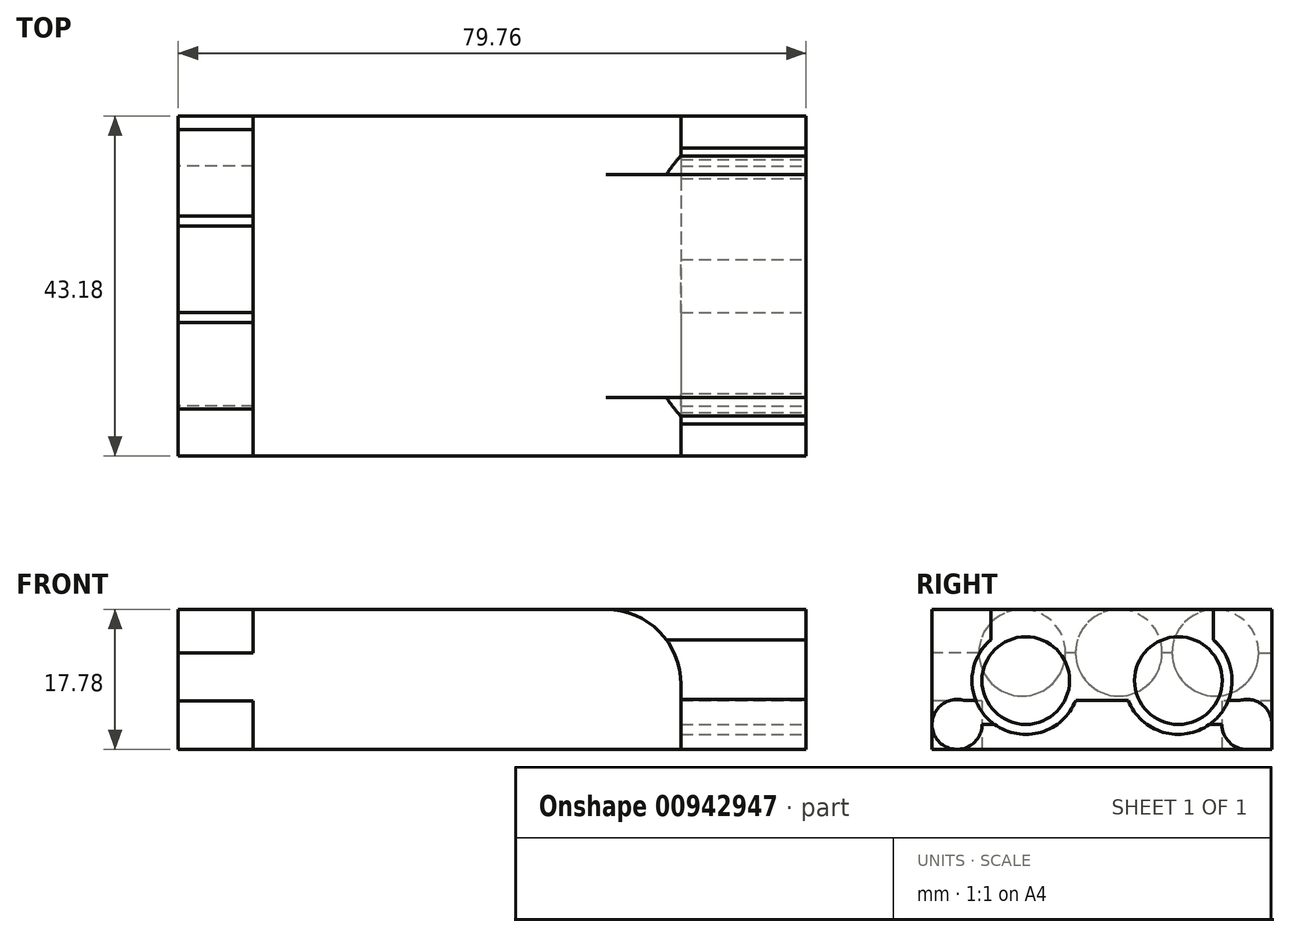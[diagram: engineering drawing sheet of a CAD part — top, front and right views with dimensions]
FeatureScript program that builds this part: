
annotation { "Feature Type Name" : "Feature", "Feature Type Description" : "" }
export const myFeature = defineFeature(function(context is Context, id is Id, definition is map)
    precondition{}
    {
        {
            var Q0;
            Q0=qCreatedBy(makeId("Top.planeOp"),FACE);
            var sketch = newSketch(context, id + "F0", { "sketchPlane" : qUnion([Q0])});
            skLineSegment(sketch, "E0", {"start": v(-39.88, 0) * mm, "end": v(-39.88, 21.59) * mm});
            skLineSegment(sketch, "E1.MirrorCS", {"start": v(39.88, 0) * mm, "end": v(39.88, 21.59) * mm});
            skLineSegment(sketch, "E2.MirrorCS", {"start": v(-39.88, 0) * mm, "end": v(-39.88, -21.59) * mm});
            skLineSegment(sketch, "E3.MirrorCS", {"start": v(39.88, 0) * mm, "end": v(39.88, -21.59) * mm});
            skLineSegment(sketch, "E4", {"start": v(-39.88, 21.59) * mm, "end": v(39.88, 21.59) * mm});
            skLineSegment(sketch, "E5", {"start": v(39.88, -21.59) * mm, "end": v(-39.88, -21.59) * mm});
            skSolve(sketch);
        }
        {
            var Q0;
            Q0=makeQuery(id+"F0.imprint","IMPRINT",FACE,{"disambiguationData":[TD([[makeQuery(id+"F0.imprint","IMPRINT",EDGE,{"derivedFrom":sQuery(id+"F0.wireOp",EDGE,"E0")}),-1.0]])]});
            extrude(context, id + "F1", {"entities" : qUnion([Q0]), "depth" : 17.78 * mm, "offsetDistance" : 25.4 * mm});
        }
        {
            var Q0;
            Q0=makeQuery(id+"F1.opExtrude","SWEPT_FACE",FACE,{"disambiguationData":[OSD([sQuery(id+"F0.wireOp",EDGE,"E0"),sQuery(id+"F0.wireOp",EDGE,"E2.MirrorCS")])]});
            var sketch = newSketch(context, id + "F2", { "sketchPlane" : qUnion([Q0])});
            skLineSegment(sketch, "E6", {"start": v(-21.59, 0) * mm, "end": v(21.59, 0) * mm});
            skLineSegment(sketch, "E7", {"start": v(-21.59, 17.78) * mm, "end": v(-21.59, 12.28) * mm});
            skCircle(sketch, "E8", {"center": v(-14.4, 12.28) * mm, "radius": 5.5 * mm});
            skLineSegment(sketch, "E9", {"start": v(-19.9, 12.28) * mm, "end": v(-21.59, 12.28) * mm});
            skLineSegment(sketch, "E10", {"start": v(13.1, 12.28) * mm, "end": v(21.59, 12.28) * mm});
            skLineSegment(sketch, "E11", {"start": v(-21.59, 0) * mm, "end": v(-21.59, 6.14) * mm});
            skLineSegment(sketch, "E12", {"start": v(-21.59, 6.14) * mm, "end": v(21.59, 6.14) * mm});
            skLineSegment(sketch, "E13", {"start": v(-21.59, 6.14) * mm, "end": v(-15.24, 6.14) * mm});
            skLineSegment(sketch, "E14.MirrorCS", {"start": v(21.59, 0) * mm, "end": v(21.59, 6.14) * mm});
            skLineSegment(sketch, "E15.MirrorCS", {"start": v(21.59, 6.14) * mm, "end": v(-21.59, 6.14) * mm});
            skLineSegment(sketch, "E16", {"start": v(21.59, 6.14) * mm, "end": v(15.24, 6.14) * mm});
            skLineSegment(sketch, "E17", {"start": v(-15.24, 6.14) * mm, "end": v(-15.24, 0) * mm});
            skLineSegment(sketch, "E18.MirrorCS", {"start": v(15.24, 6.14) * mm, "end": v(15.24, 0) * mm});
            skLineSegment(sketch, "E19", {"start": v(-8.9, 12.28) * mm, "end": v(-7.63, 12.28) * mm});
            skCircle(sketch, "E20.MirrorC", {"center": v(-2.13, 12.28) * mm, "radius": 5.5 * mm});
            skCircle(sketch, "E21.MirrorC", {"center": v(10.14, 12.28) * mm, "radius": 5.5 * mm});
            skLineSegment(sketch, "E22", {"start": v(3.37, 12.28) * mm, "end": v(4.64, 12.28) * mm});
            skSolve(sketch);
        }
        {
            var Q0;
            {var subQ0=sQuery(id+"F2.wireOp",EDGE,"E7");Q0=makeQuery(id+"F2.imprint","IMPRINT",FACE,{"disambiguationData":[TD([[makeQuery(id+"F2.imprint","IMPRINT",EDGE,{"derivedFrom":subQ0}),1.0]])]});}
            var Q1;
            {var subQ0=sQuery(id+"F2.wireOp",EDGE,"11ba6505-8bd9-4545-8600-2fb35892f41e0.MirrorC");var subQ1=sQuery(id+"F2.wireOp",EDGE,"E8");var subQ2=makeQuery(id+"F2.imprint","INTERSECT",VERTEX,{"derivedFrom":[subQ1,subQ0]});Q1=makeQuery(id+"F2.imprint","IMPRINT",FACE,{"disambiguationData":[TD([[makeQuery(id+"F2.imprint","IMPRINT",EDGE,{"disambiguationData":[TD([[subQ2,-1.0]])],"derivedFrom":subQ1}),-1.0]])]});}
            var Q2;
            {var subQ0=sQuery(id+"F2.wireOp",EDGE,"8c5e6d80-e282-41b0-858f-738f4d739d140.MirrorC");var subQ1=sQuery(id+"F2.wireOp",EDGE,"11ba6505-8bd9-4545-8600-2fb35892f41e0.MirrorC");var subQ2=makeQuery(id+"F2.imprint","INTERSECT",VERTEX,{"derivedFrom":[subQ1,subQ0]});Q2=makeQuery(id+"F2.imprint","IMPRINT",FACE,{"disambiguationData":[TD([[makeQuery(id+"F2.imprint","IMPRINT",EDGE,{"disambiguationData":[TD([[subQ2,1.0]])],"derivedFrom":subQ1}),1.0]])]});}
            var Q3;
            {var subQ0=sQuery(id+"F2.wireOp",EDGE,"E10");Q3=makeQuery(id+"F2.imprint","IMPRINT",FACE,{"disambiguationData":[TD([[makeQuery(id+"F2.imprint","IMPRINT",EDGE,{"derivedFrom":subQ0}),1.0]])]});}
            var Q4;
            {var subQ0=sQuery(id+"F2.wireOp",EDGE,"E11");Q4=makeQuery(id+"F2.imprint","IMPRINT",FACE,{"disambiguationData":[TD([[makeQuery(id+"F2.imprint","IMPRINT",EDGE,{"derivedFrom":subQ0}),1.0]])]});}
            var Q5;
            {var subQ0=sQuery(id+"F2.wireOp",EDGE,"E14.MirrorCS");Q5=makeQuery(id+"F2.imprint","IMPRINT",FACE,{"disambiguationData":[TD([[makeQuery(id+"F2.imprint","IMPRINT",EDGE,{"derivedFrom":subQ0}),-1.0]])]});}
            var Q6;
            {var subQ0=sQuery(id+"F2.wireOp",EDGE,"E22");Q6=makeQuery(id+"F2.imprint","IMPRINT",FACE,{"disambiguationData":[TD([[makeQuery(id+"F2.imprint","IMPRINT",EDGE,{"derivedFrom":subQ0}),1.0]])]});}
            extrude(context, id + "F3", {"entities" : qUnion([Q0, Q1, Q2, Q3, Q4, Q5, Q6]), "operationType" : NewBodyOperationType.REMOVE, "oppositeDirection" : true, "depth" : 9.52 * mm, "offsetDistance" : 25.4 * mm});
        }
        {
            var Q0;
            {var subQ0=sQuery(id+"F2.wireOp",EDGE,"E17");Q0=makeQuery(id+"F2.imprint","IMPRINT",FACE,{"disambiguationData":[TD([[makeQuery(id+"F2.imprint","IMPRINT",EDGE,{"derivedFrom":subQ0}),1.0]])]});}
            var Q1;
            {var subQ0=sQuery(id+"F2.wireOp",EDGE,"E9");Q1=makeQuery(id+"F2.imprint","IMPRINT",FACE,{"disambiguationData":[TD([[makeQuery(id+"F2.imprint","IMPRINT",EDGE,{"derivedFrom":subQ0}),1.0]])]});}
            extrude(context, id + "F4", {"entities" : qUnion([Q0, Q1]), "operationType" : NewBodyOperationType.REMOVE, "oppositeDirection" : true, "depth" : 3 / 406.4 * mm, "offsetDistance" : 25.4 * mm});
        }
        {
            var Q0;
            Q0=makeQuery(id+"F1.opExtrude","SWEPT_FACE",FACE,{"disambiguationData":[OSD([sQuery(id+"F0.wireOp",EDGE,"E1.MirrorCS"),sQuery(id+"F0.wireOp",EDGE,"E3.MirrorCS")])]});
            var sketch = newSketch(context, id + "F5", { "sketchPlane" : qUnion([Q0])});
            skLineSegment(sketch, "E23", {"start": v(-21.59, 0) * mm, "end": v(-21.59, 3.18) * mm});
            skLineSegment(sketch, "E24", {"start": v(-21.59, 0) * mm, "end": v(-12.04, 0) * mm});
            skLineSegment(sketch, "E25", {"start": v(-21.59, 0) * mm, "end": v(21.59, 0) * mm});
            skLineSegment(sketch, "E26", {"start": v(21.59, 0) * mm, "end": v(-21.59, 0) * mm});
            skLineSegment(sketch, "E27", {"start": v(-21.59, 3.18) * mm, "end": v(-18.41, 3.18) * mm});
            skCircle(sketch, "E28", {"center": v(-18.41, 3.18) * mm, "radius": 3.18 * mm});
            skLineSegment(sketch, "E29", {"start": v(-15.24, 3.18) * mm, "end": v(-13.65, 3.18) * mm});
            skCircle(sketch, "E30", {"center": v(-9.69, 8.74) * mm, "radius": 5.57 * mm});
            skCircle(sketch, "E31.MirrorC", {"center": v(9.69, 8.74) * mm, "radius": 5.57 * mm});
            skArc(sketch, "E32", {"start": v(-3.34, 11.27) * mm, "mid": v(-16.52, 8.74) * mm, "end": v(-3.34, 6.21) * mm});
            skArc(sketch, "E33.MirrorC", {"start": v(3.34, 11.27) * mm, "mid": v(16.52, 8.74) * mm, "end": v(3.34, 6.21) * mm});
            skCircle(sketch, "E34.MirrorC", {"center": v(18.41, 3.18) * mm, "radius": 3.18 * mm});
            skLineSegment(sketch, "E35", {"start": v(-3.34, 6.21) * mm, "end": v(3.34, 6.21) * mm});
            skLineSegment(sketch, "E36", {"start": v(-9.69, 8.74) * mm, "end": v(-6.73, 8.74) * mm});
            skLineSegment(sketch, "E37.MirrorCS", {"start": v(-3.34, 11.27) * mm, "end": v(3.34, 11.27) * mm});
            skLineSegment(sketch, "E38", {"start": v(-14.14, 13.93) * mm, "end": v(-14.14, 17.78) * mm});
            skLineSegment(sketch, "E39.MirrorCS", {"start": v(14.14, 13.93) * mm, "end": v(14.14, 17.78) * mm});
            skPoint(sketch, "E40.trimOffspring.end.orphan", {"position": v(-9.68, 3.19) * mm});
            skLineSegment(sketch, "E41.MirrorCS", {"start": v(15.24, 3.18) * mm, "end": v(13.65, 3.18) * mm});
            skLineSegment(sketch, "E42", {"start": v(-17.52, 6.22) * mm, "end": v(-16.04, 6.22) * mm});
            skLineSegment(sketch, "E43.MirrorCS", {"start": v(17.52, 6.22) * mm, "end": v(16.04, 6.22) * mm});
            skSolve(sketch);
        }
        {
            var Q0;
            {var subQ1=sQuery(id+"F5.wireOp",EDGE,"E37.MirrorCS");Q0=makeQuery(id+"F5.imprint","IMPRINT",FACE,{"disambiguationData":[TD([[makeQuery(id+"F5.imprint","IMPRINT",EDGE,{"derivedFrom":subQ1}),1.0]])]});}
            var Q1;
            Q1=makeQuery(id+"F5.imprint","IMPRINT",FACE,{"disambiguationData":[TD([[makeQuery(id+"F5.imprint","IMPRINT",EDGE,{"derivedFrom":sQuery(id+"F5.wireOp",EDGE,"E30")}),-1.0]])]});
            extrude(context, id + "F6", {"entities" : qUnion([Q0, Q1]), "operationType" : NewBodyOperationType.REMOVE, "oppositeDirection" : true, "depth" : 3 / 406.4 * mm, "offsetDistance" : 25.4 * mm});
        }
        {
            var Q0;
            {var subQ0=sQuery(id+"F5.wireOp",EDGE,"E29");Q0=makeQuery(id+"F5.imprint","IMPRINT",FACE,{"disambiguationData":[TD([[makeQuery(id+"F5.imprint","IMPRINT",EDGE,{"derivedFrom":subQ0}),-1.0]])]});}
            extrude(context, id + "F7", {"entities" : qUnion([Q0]), "operationType" : NewBodyOperationType.REMOVE, "oppositeDirection" : true, "depth" : 17.46 * mm, "offsetDistance" : 25.4 * mm});
        }
        {
            var Q0;
            {var subQ1=sQuery(id+"F5.wireOp",EDGE,"E38");Q0=makeQuery(id+"F5.imprint","IMPRINT",FACE,{"disambiguationData":[TD([[makeQuery(id+"F5.imprint","IMPRINT",EDGE,{"derivedFrom":subQ1}),1.0]])]});}
            var Q1;
            {var subQ5=sQuery(id+"F5.wireOp",EDGE,"E39.MirrorCS");Q1=makeQuery(id+"F5.imprint","IMPRINT",FACE,{"disambiguationData":[TD([[makeQuery(id+"F5.imprint","IMPRINT",EDGE,{"derivedFrom":subQ5}),-1.0]])]});}
            extrude(context, id + "F8", {"entities" : qUnion([Q0, Q1]), "operationType" : NewBodyOperationType.REMOVE, "oppositeDirection" : true, "depth" : 25.4 * mm, "offsetDistance" : 25.4 * mm});
        }
        {
            var Q0;
            {var subQ0=sQuery(id+"F5.wireOp",EDGE,"E23");Q0=makeQuery(id+"F5.imprint","IMPRINT",FACE,{"disambiguationData":[TD([[makeQuery(id+"F5.imprint","IMPRINT",EDGE,{"derivedFrom":subQ0}),1.0]])]});}
            var Q1;
            {var subQ0=sQuery(id+"F5.wireOp",EDGE,"E26");var subQ3=sQuery(id+"F5.wireOp",EDGE,"E34.MirrorC");var subQ4=makeQuery(id+"F5.imprint","INTERSECT",VERTEX,{"derivedFrom":[subQ0,subQ3]});Q1=makeQuery(id+"F5.imprint","IMPRINT",FACE,{"disambiguationData":[TD([[makeQuery(id+"F5.imprint","IMPRINT",EDGE,{"disambiguationData":[TD([[subQ4,1.0]])],"derivedFrom":subQ0}),-1.0]])]});}
            extrude(context, id + "F9", {"entities" : qUnion([Q0, Q1]), "operationType" : NewBodyOperationType.REMOVE, "oppositeDirection" : true, "depth" : 15.88 * mm, "offsetDistance" : 25.4 * mm});
        }
        {
            var Q0;
            Q0=makeQuery(id+"F1.opExtrude","SWEPT_FACE",FACE,{"disambiguationData":[OSD([sQuery(id+"F0.wireOp",EDGE,"E5")])]});
            var sketch = newSketch(context, id + "F10", { "sketchPlane" : qUnion([Q0])});
            skLineSegment(sketch, "E44", {"start": v(14.48, 17.78) * mm, "end": v(14.48, 8.26) * mm});
            skLineSegment(sketch, "E45", {"start": v(14.48, 8.26) * mm, "end": v(24, 8.26) * mm});
            skArc(sketch, "E46", {"start": v(14.48, 17.78) * mm, "mid": v(21.21, 15) * mm, "end": v(24, 8.26) * mm});
            skLineSegment(sketch, "E47", {"start": v(24, 8.26) * mm, "end": v(24, 0) * mm});
            skLineSegment(sketch, "E48", {"start": v(24, 0) * mm, "end": v(14.48, 0) * mm});
            skLineSegment(sketch, "E49", {"start": v(14.48, 0) * mm, "end": v(14.48, 8.26) * mm});
            skSolve(sketch);
        }
        {
            var Q0;
            Q0=makeQuery(id+"F10.imprint","IMPRINT",FACE,{"disambiguationData":[TD([[makeQuery(id+"F10.imprint","IMPRINT",EDGE,{"derivedFrom":sQuery(id+"F10.wireOp",EDGE,"E44")}),1.0]])]});
            var Q1;
            {var subQ0=sQuery(id+"F10.wireOp",EDGE,"E45");Q1=makeQuery(id+"F10.imprint","IMPRINT",FACE,{"disambiguationData":[TD([[makeQuery(id+"F10.imprint","IMPRINT",EDGE,{"derivedFrom":subQ0}),-1.0]])]});}
            var Q2;
            {var subQ0=sQuery(id+"F10.wireOp",EDGE,"E48");Q2=makeQuery(id+"F10.imprint","IMPRINT",FACE,{"disambiguationData":[TD([[makeQuery(id+"F10.imprint","IMPRINT",EDGE,{"derivedFrom":subQ0}),-1.0]])]});}
            extrude(context, id + "F11", {"entities" : qUnion([Q0, Q1, Q2]), "operationType" : NewBodyOperationType.ADD, "oppositeDirection" : true, "depth" : 43.18 * mm, "offsetDistance" : 25.4 * mm});
        }
    });
